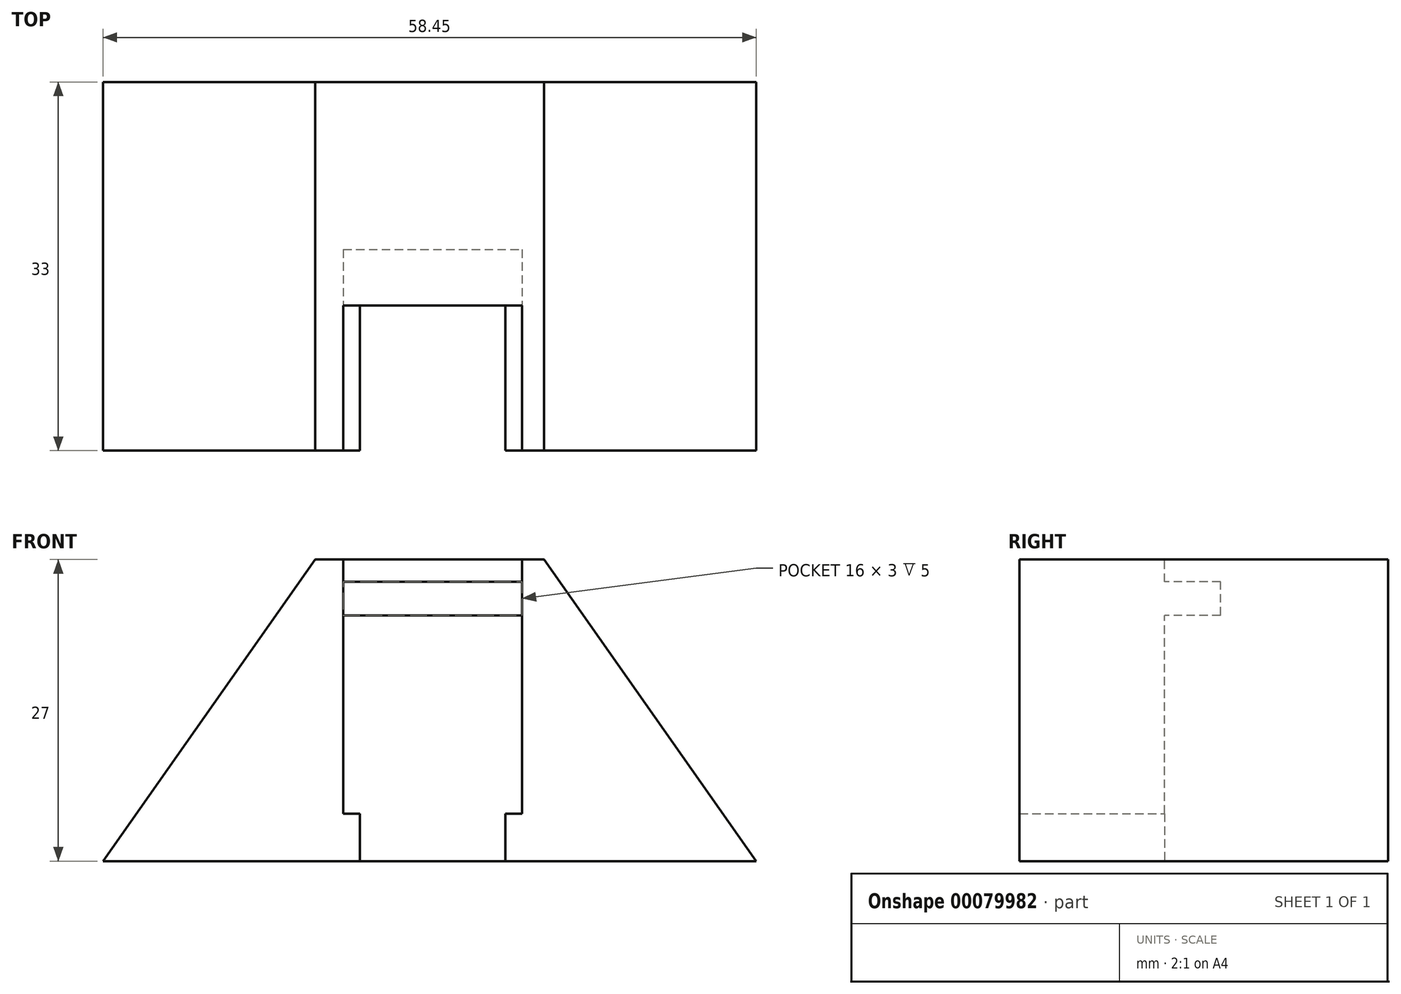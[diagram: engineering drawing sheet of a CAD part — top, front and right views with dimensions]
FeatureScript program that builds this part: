
annotation { "Feature Type Name" : "Feature", "Feature Type Description" : "" }
export const myFeature = defineFeature(function(context is Context, id is Id, definition is map)
    precondition{}
    {
        {
            var Q0;
            Q0=qCreatedBy(makeId("Top.planeOp"),FACE);
            var sketch = newSketch(context, id + "F0", { "sketchPlane" : qUnion([Q0])});
            skLineSegment(sketch, "E0.bottom", {"start": v(-29.5, 33) * mm, "end": v(28.95, 33) * mm});
            skLineSegment(sketch, "E0.top", {"start": v(-29.5, 0) * mm, "end": v(-6.5, 0) * mm});
            skLineSegment(sketch, "E0.left", {"start": v(-29.5, 33) * mm, "end": v(-29.5, 0) * mm});
            skLineSegment(sketch, "E0.right", {"start": v(28.95, 33) * mm, "end": v(28.95, 0) * mm});
            skLineSegment(sketch, "E1", {"start": v(-6.5, 0) * mm, "end": v(-6.5, 13) * mm});
            skLineSegment(sketch, "E2", {"start": v(6.5, 0) * mm, "end": v(6.5, 13) * mm});
            skLineSegment(sketch, "E3", {"start": v(6.5, 13) * mm, "end": v(-6.5, 13) * mm});
            skLineSegment(sketch, "E4.trimOffspring", {"start": v(6.5, 0) * mm, "end": v(28.95, 0) * mm});
            skSolve(sketch);
        }
        {
            var Q0;
            Q0 = qSketchRegion(id + "F0", true);
            extrude(context, id + "F1", {"entities" : qUnion([Q0]), "depth" : 27 * mm});
        }
        {
            var Q0;
            Q0=makeQuery(id+"F1.opExtrude","SWEPT_FACE",FACE,{"disambiguationData":[OSD([sQuery(id+"F0.wireOp",EDGE,"E0.top")])]});
            var sketch = newSketch(context, id + "F2", { "sketchPlane" : qUnion([Q0])});
            skLineSegment(sketch, "E5", {"start": v(-10.52, 27) * mm, "end": v(-29.5, 0) * mm});
            skLineSegment(sketch, "E6", {"start": v(-29.5, 0) * mm, "end": v(-29.5, 27) * mm});
            skLineSegment(sketch, "E7", {"start": v(-29.45, 27) * mm, "end": v(-6.45, 27) * mm});
            skLineSegment(sketch, "E8", {"start": v(28.95, 27) * mm, "end": v(28.95, 0) * mm});
            skLineSegment(sketch, "E9", {"start": v(28.95, 0) * mm, "end": v(9.97, 27) * mm});
            skLineSegment(sketch, "E10", {"start": v(9.97, 27) * mm, "end": v(28.95, 27) * mm});
            skSolve(sketch);
        }
        {
            var Q0;
            Q0 = qSketchRegion(id + "F2", true);
            var Q1;
            {var subQ0=sQuery(id+"F2.wireOp",EDGE,"E5");Q1=makeQuery(id+"F2.imprint","IMPRINT",FACE,{"disambiguationData":[TD([[makeQuery(id+"F2.imprint","IMPRINT",EDGE,{"derivedFrom":subQ0}),-1.0]])]});}
            var Q2;
            Q2=makeQuery(id+"F1.opExtrude","SWEPT_FACE",FACE,{"disambiguationData":[OSD([sQuery(id+"F0.wireOp",EDGE,"E0.bottom")])]});
            extrude(context, id + "F3", {"entities" : qUnion([Q0, Q1]), "operationType" : NewBodyOperationType.REMOVE, "endBound" : BoundingType.UP_TO_SURFACE, "oppositeDirection" : true, "endBoundEntityFace" : qUnion([Q2]), "depth" : 25 * mm});
        }
        {
            var Q0;
            Q0=makeQuery(id+"F1.opExtrude","CAP_FACE",FACE,{"disambiguationData":[OSD([sQuery(id+"F0.wireOp",EDGE,"E0.bottom"),sQuery(id+"F0.wireOp",EDGE,"E0.top"),sQuery(id+"F0.wireOp",EDGE,"E0.left"),sQuery(id+"F0.wireOp",EDGE,"E0.right"),sQuery(id+"F0.wireOp",EDGE,"E1"),sQuery(id+"F0.wireOp",EDGE,"E2"),sQuery(id+"F0.wireOp",EDGE,"E3"),sQuery(id+"F0.wireOp",EDGE,"E4.trimOffspring")])],"isStart":false});
            var sketch = newSketch(context, id + "F4", { "sketchPlane" : qUnion([Q0])});
            skLineSegment(sketch, "E11", {"start": v(-6.5, 13) * mm, "end": v(-8, 13) * mm});
            skLineSegment(sketch, "E12", {"start": v(6.5, 13) * mm, "end": v(8, 13) * mm});
            skLineSegment(sketch, "E13", {"start": v(8, 13) * mm, "end": v(8, 0) * mm});
            skLineSegment(sketch, "E14", {"start": v(8, 0) * mm, "end": v(6.5, 0) * mm});
            skLineSegment(sketch, "E15", {"start": v(6.5, 0) * mm, "end": v(6.5, 13) * mm});
            skLineSegment(sketch, "E16", {"start": v(-8, 13) * mm, "end": v(-8, 0) * mm});
            skLineSegment(sketch, "E17", {"start": v(-8, 0) * mm, "end": v(-6.5, 0) * mm});
            skLineSegment(sketch, "E18", {"start": v(-6.5, 0) * mm, "end": v(-6.5, 13) * mm});
            skSolve(sketch);
        }
        {
            var Q0;
            Q0 = qSketchRegion(id + "F4", true);
            extrude(context, id + "F5", {"entities" : qUnion([Q0]), "operationType" : NewBodyOperationType.REMOVE, "oppositeDirection" : true, "depth" : 22.75 * mm});
        }
        {
            var Q0;
            Q0=makeQuery(id+"F5.boolean.opBoolean","MERGE",FACE,{"derivedFrom":[makeQuery(id+"F1.opExtrude","SWEPT_FACE",FACE,{"disambiguationData":[OSD([sQuery(id+"F0.wireOp",EDGE,"E3")])]}),makeQuery(id+"F5.opExtrude","SWEPT_FACE",FACE,{"disambiguationData":[OSD([sQuery(id+"F4.wireOp",EDGE,"E11")])]}),makeQuery(id+"F5.opExtrude","SWEPT_FACE",FACE,{"disambiguationData":[OSD([sQuery(id+"F4.wireOp",EDGE,"E12")])]})]});
            var sketch = newSketch(context, id + "F6", { "sketchPlane" : qUnion([Q0])});
            skLineSegment(sketch, "E19", {"start": v(-8, 25) * mm, "end": v(8, 25) * mm});
            skLineSegment(sketch, "E20", {"start": v(8, 25) * mm, "end": v(8, 22) * mm});
            skLineSegment(sketch, "E21", {"start": v(8, 22) * mm, "end": v(-8, 22) * mm});
            skLineSegment(sketch, "E22", {"start": v(-8, 22) * mm, "end": v(-8, 25) * mm});
            skSolve(sketch);
        }
        {
            var Q0;
            Q0 = qSketchRegion(id + "F6", true);
            extrude(context, id + "F7", {"entities" : qUnion([Q0]), "operationType" : NewBodyOperationType.REMOVE, "oppositeDirection" : true, "depth" : 5 * mm});
        }
    });
